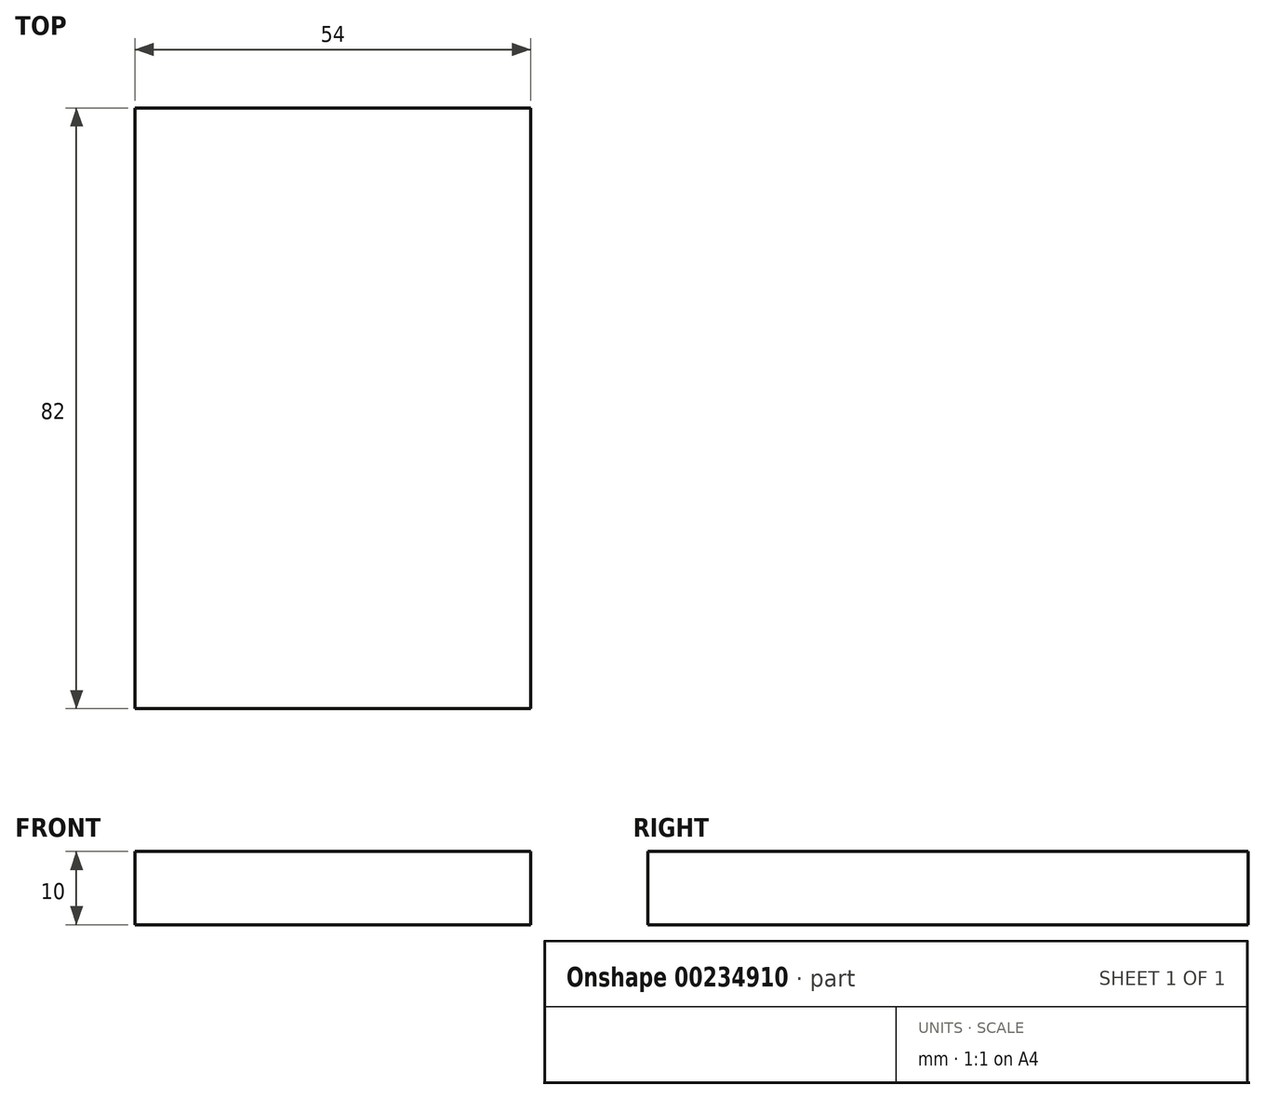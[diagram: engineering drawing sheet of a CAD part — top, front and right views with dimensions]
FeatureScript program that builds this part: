
annotation { "Feature Type Name" : "Feature", "Feature Type Description" : "" }
export const myFeature = defineFeature(function(context is Context, id is Id, definition is map)
    precondition{}
    {
        {
            var Q0;
            Q0=qCreatedBy(makeId("Top.planeOp"),FACE);
            var sketch = newSketch(context, id + "F0", { "sketchPlane" : qUnion([Q0])});
            skLineSegment(sketch, "E0.bottom", {"start": v(27, 41) * mm, "end": v(-27, 41) * mm});
            skLineSegment(sketch, "E0.top", {"start": v(27, -41) * mm, "end": v(-27, -41) * mm});
            skLineSegment(sketch, "E0.left", {"start": v(27, 41) * mm, "end": v(27, -41) * mm});
            skLineSegment(sketch, "E0.right", {"start": v(-27, 41) * mm, "end": v(-27, -41) * mm});
            skPoint(sketch, "E0.middle", {"position": v(0, 0) * mm});
            skSolve(sketch);
        }
        {
            var Q0;
            Q0 = qSketchRegion(id + "F0", true);
            extrude(context, id + "F1", {"entities" : qUnion([Q0]), "depth" : 10 * mm, "offsetDistance" : 25 * mm});
        }
    });
